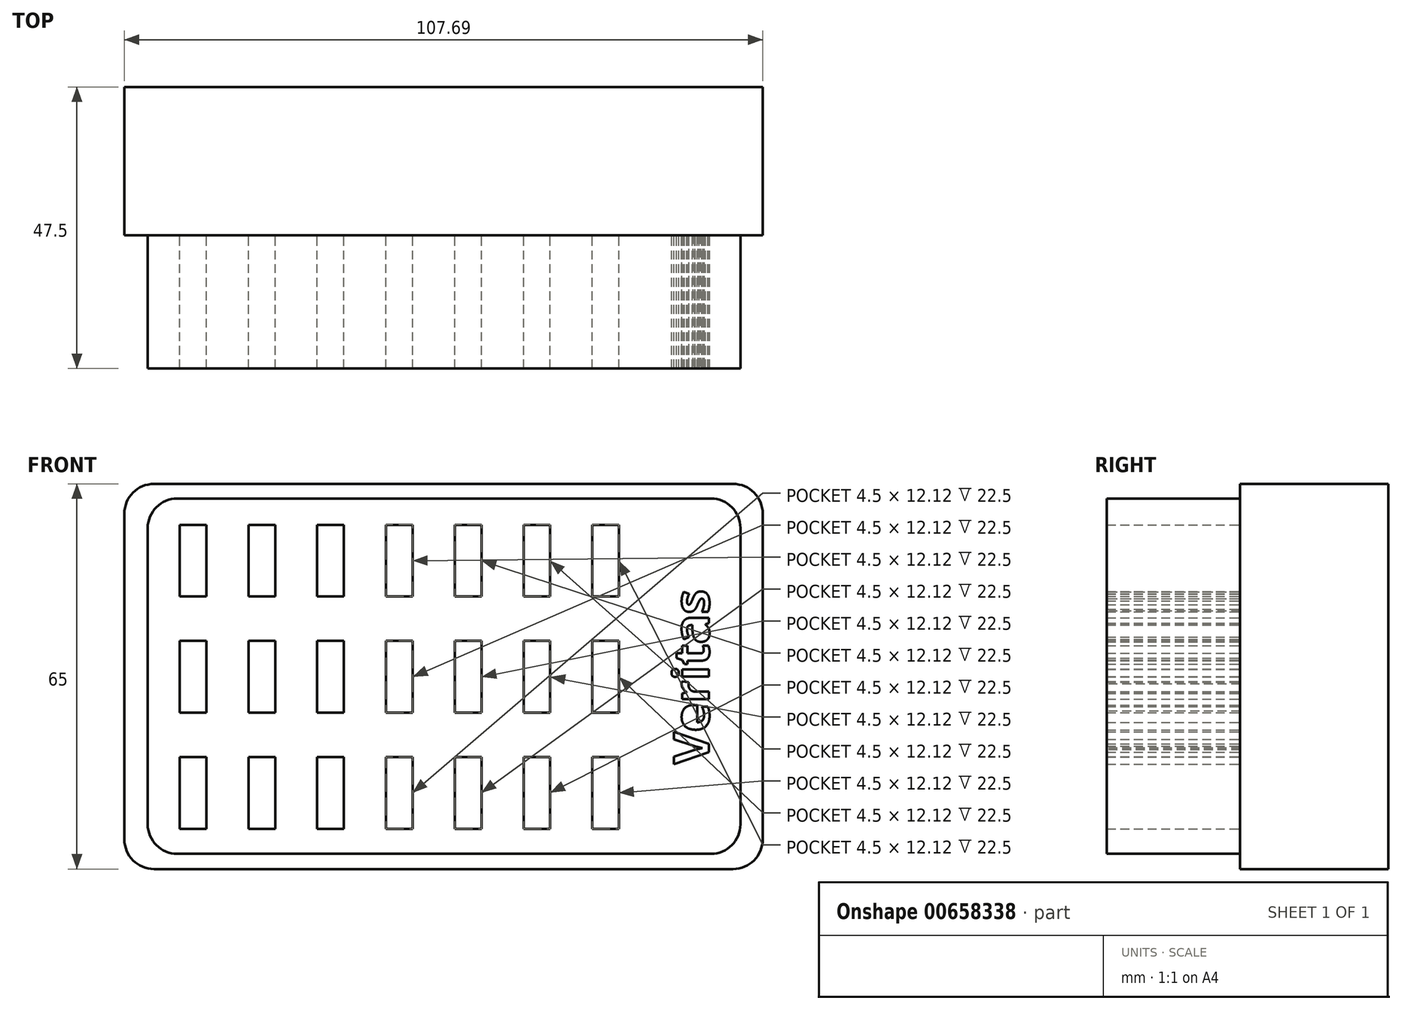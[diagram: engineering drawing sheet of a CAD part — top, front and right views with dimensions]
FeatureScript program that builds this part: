
annotation { "Feature Type Name" : "Feature", "Feature Type Description" : "" }
export const myFeature = defineFeature(function(context is Context, id is Id, definition is map)
    precondition{}
    {
        {
            var Q0;
            Q0=qCreatedBy(makeId("Front.planeOp"),FACE);
            var sketch = newSketch(context, id + "F0", { "sketchPlane" : qUnion([Q0])});
            skLineSegment(sketch, "E0.bottom", {"start": v(50, 30) * mm, "end": v(-50, 30) * mm});
            skLineSegment(sketch, "E0.top", {"start": v(50, -30) * mm, "end": v(-50, -30) * mm});
            skLineSegment(sketch, "E0.left", {"start": v(50, 30) * mm, "end": v(50, -30) * mm});
            skLineSegment(sketch, "E0.right", {"start": v(-50, 30) * mm, "end": v(-50, -30) * mm});
            skPoint(sketch, "E0.middle", {"position": v(0, 0) * mm});
            skLineSegment(sketch, "E1.bottom", {"start": v(-44.6, -13.64) * mm, "end": v(-40.1, -13.64) * mm});
            skLineSegment(sketch, "E1.top", {"start": v(-44.6, -25.76) * mm, "end": v(-40.1, -25.76) * mm});
            skLineSegment(sketch, "E1.left", {"start": v(-44.6, -13.64) * mm, "end": v(-44.6, -25.76) * mm});
            skLineSegment(sketch, "E1.right", {"start": v(-40.1, -13.64) * mm, "end": v(-40.1, -25.76) * mm});
            skLineSegment(sketch, "E2.0.1.0", {"start": v(-40.1, 5.96) * mm, "end": v(-40.1, -6.16) * mm});
            skLineSegment(sketch, "E2.0.1.1", {"start": v(-44.6, 5.96) * mm, "end": v(-44.6, -6.16) * mm});
            skLineSegment(sketch, "E2.0.1.2", {"start": v(-44.6, -6.16) * mm, "end": v(-40.1, -6.16) * mm});
            skLineSegment(sketch, "E2.0.1.3", {"start": v(-44.6, 5.96) * mm, "end": v(-40.1, 5.96) * mm});
            skLineSegment(sketch, "E2.0.2.0", {"start": v(-40.1, 25.56) * mm, "end": v(-40.1, 13.44) * mm});
            skLineSegment(sketch, "E2.0.2.1", {"start": v(-44.6, 25.56) * mm, "end": v(-44.6, 13.44) * mm});
            skLineSegment(sketch, "E2.0.2.2", {"start": v(-44.6, 13.44) * mm, "end": v(-40.1, 13.44) * mm});
            skLineSegment(sketch, "E2.0.2.3", {"start": v(-44.6, 25.56) * mm, "end": v(-40.1, 25.56) * mm});
            skLineSegment(sketch, "E2.1.0.0", {"start": v(-28.5, -13.64) * mm, "end": v(-28.5, -25.76) * mm});
            skLineSegment(sketch, "E2.1.0.1", {"start": v(-33, -13.64) * mm, "end": v(-33, -25.76) * mm});
            skLineSegment(sketch, "E2.1.0.2", {"start": v(-33, -25.76) * mm, "end": v(-28.5, -25.76) * mm});
            skLineSegment(sketch, "E2.1.0.3", {"start": v(-33, -13.64) * mm, "end": v(-28.5, -13.64) * mm});
            skLineSegment(sketch, "E2.1.1.0", {"start": v(-28.5, 5.96) * mm, "end": v(-28.5, -6.16) * mm});
            skLineSegment(sketch, "E2.1.1.1", {"start": v(-33, 5.96) * mm, "end": v(-33, -6.16) * mm});
            skLineSegment(sketch, "E2.1.1.2", {"start": v(-33, -6.16) * mm, "end": v(-28.5, -6.16) * mm});
            skLineSegment(sketch, "E2.1.1.3", {"start": v(-33, 5.96) * mm, "end": v(-28.5, 5.96) * mm});
            skLineSegment(sketch, "E2.1.2.0", {"start": v(-28.5, 25.56) * mm, "end": v(-28.5, 13.44) * mm});
            skLineSegment(sketch, "E2.1.2.1", {"start": v(-33, 25.56) * mm, "end": v(-33, 13.44) * mm});
            skLineSegment(sketch, "E2.1.2.2", {"start": v(-33, 13.44) * mm, "end": v(-28.5, 13.44) * mm});
            skLineSegment(sketch, "E2.1.2.3", {"start": v(-33, 25.56) * mm, "end": v(-28.5, 25.56) * mm});
            skLineSegment(sketch, "E2.2.0.0", {"start": v(-16.9, -13.64) * mm, "end": v(-16.9, -25.76) * mm});
            skLineSegment(sketch, "E2.2.0.1", {"start": v(-21.4, -13.64) * mm, "end": v(-21.4, -25.76) * mm});
            skLineSegment(sketch, "E2.2.0.2", {"start": v(-21.4, -25.76) * mm, "end": v(-16.9, -25.76) * mm});
            skLineSegment(sketch, "E2.2.0.3", {"start": v(-21.4, -13.64) * mm, "end": v(-16.9, -13.64) * mm});
            skLineSegment(sketch, "E2.2.1.0", {"start": v(-16.9, 5.96) * mm, "end": v(-16.9, -6.16) * mm});
            skLineSegment(sketch, "E2.2.1.1", {"start": v(-21.4, 5.96) * mm, "end": v(-21.4, -6.16) * mm});
            skLineSegment(sketch, "E2.2.1.2", {"start": v(-21.4, -6.16) * mm, "end": v(-16.9, -6.16) * mm});
            skLineSegment(sketch, "E2.2.1.3", {"start": v(-21.4, 5.96) * mm, "end": v(-16.9, 5.96) * mm});
            skLineSegment(sketch, "E2.2.2.0", {"start": v(-16.9, 25.56) * mm, "end": v(-16.9, 13.44) * mm});
            skLineSegment(sketch, "E2.2.2.1", {"start": v(-21.4, 25.56) * mm, "end": v(-21.4, 13.44) * mm});
            skLineSegment(sketch, "E2.2.2.2", {"start": v(-21.4, 13.44) * mm, "end": v(-16.9, 13.44) * mm});
            skLineSegment(sketch, "E2.2.2.3", {"start": v(-21.4, 25.56) * mm, "end": v(-16.9, 25.56) * mm});
            skLineSegment(sketch, "E2.3.0.0", {"start": v(-5.3, -13.64) * mm, "end": v(-5.3, -25.76) * mm});
            skLineSegment(sketch, "E2.3.0.1", {"start": v(-9.8, -13.64) * mm, "end": v(-9.8, -25.76) * mm});
            skLineSegment(sketch, "E2.3.0.2", {"start": v(-9.8, -25.76) * mm, "end": v(-5.3, -25.76) * mm});
            skLineSegment(sketch, "E2.3.0.3", {"start": v(-9.8, -13.64) * mm, "end": v(-5.3, -13.64) * mm});
            skLineSegment(sketch, "E2.3.1.0", {"start": v(-5.3, 5.96) * mm, "end": v(-5.3, -6.16) * mm});
            skLineSegment(sketch, "E2.3.1.1", {"start": v(-9.8, 5.96) * mm, "end": v(-9.8, -6.16) * mm});
            skLineSegment(sketch, "E2.3.1.2", {"start": v(-9.8, -6.16) * mm, "end": v(-5.3, -6.16) * mm});
            skLineSegment(sketch, "E2.3.1.3", {"start": v(-9.8, 5.96) * mm, "end": v(-5.3, 5.96) * mm});
            skLineSegment(sketch, "E2.3.2.0", {"start": v(-5.3, 25.56) * mm, "end": v(-5.3, 13.44) * mm});
            skLineSegment(sketch, "E2.3.2.1", {"start": v(-9.8, 25.56) * mm, "end": v(-9.8, 13.44) * mm});
            skLineSegment(sketch, "E2.3.2.2", {"start": v(-9.8, 13.44) * mm, "end": v(-5.3, 13.44) * mm});
            skLineSegment(sketch, "E2.3.2.3", {"start": v(-9.8, 25.56) * mm, "end": v(-5.3, 25.56) * mm});
            skLineSegment(sketch, "E2.4.0.0", {"start": v(6.3, -13.64) * mm, "end": v(6.3, -25.76) * mm});
            skLineSegment(sketch, "E2.4.0.1", {"start": v(1.8, -13.64) * mm, "end": v(1.8, -25.76) * mm});
            skLineSegment(sketch, "E2.4.0.2", {"start": v(1.8, -25.76) * mm, "end": v(6.3, -25.76) * mm});
            skLineSegment(sketch, "E2.4.0.3", {"start": v(1.8, -13.64) * mm, "end": v(6.3, -13.64) * mm});
            skLineSegment(sketch, "E2.4.1.0", {"start": v(6.3, 5.96) * mm, "end": v(6.3, -6.16) * mm});
            skLineSegment(sketch, "E2.4.1.1", {"start": v(1.8, 5.96) * mm, "end": v(1.8, -6.16) * mm});
            skLineSegment(sketch, "E2.4.1.2", {"start": v(1.8, -6.16) * mm, "end": v(6.3, -6.16) * mm});
            skLineSegment(sketch, "E2.4.1.3", {"start": v(1.8, 5.96) * mm, "end": v(6.3, 5.96) * mm});
            skLineSegment(sketch, "E2.4.2.0", {"start": v(6.3, 25.56) * mm, "end": v(6.3, 13.44) * mm});
            skLineSegment(sketch, "E2.4.2.1", {"start": v(1.8, 25.56) * mm, "end": v(1.8, 13.44) * mm});
            skLineSegment(sketch, "E2.4.2.2", {"start": v(1.8, 13.44) * mm, "end": v(6.3, 13.44) * mm});
            skLineSegment(sketch, "E2.4.2.3", {"start": v(1.8, 25.56) * mm, "end": v(6.3, 25.56) * mm});
            skLineSegment(sketch, "E2.5.0.0", {"start": v(17.9, -13.64) * mm, "end": v(17.9, -25.76) * mm});
            skLineSegment(sketch, "E2.5.0.1", {"start": v(13.4, -13.64) * mm, "end": v(13.4, -25.76) * mm});
            skLineSegment(sketch, "E2.5.0.2", {"start": v(13.4, -25.76) * mm, "end": v(17.9, -25.76) * mm});
            skLineSegment(sketch, "E2.5.0.3", {"start": v(13.4, -13.64) * mm, "end": v(17.9, -13.64) * mm});
            skLineSegment(sketch, "E2.5.1.0", {"start": v(17.9, 5.96) * mm, "end": v(17.9, -6.16) * mm});
            skLineSegment(sketch, "E2.5.1.1", {"start": v(13.4, 5.96) * mm, "end": v(13.4, -6.16) * mm});
            skLineSegment(sketch, "E2.5.1.2", {"start": v(13.4, -6.16) * mm, "end": v(17.9, -6.16) * mm});
            skLineSegment(sketch, "E2.5.1.3", {"start": v(13.4, 5.96) * mm, "end": v(17.9, 5.96) * mm});
            skLineSegment(sketch, "E2.5.2.0", {"start": v(17.9, 25.56) * mm, "end": v(17.9, 13.44) * mm});
            skLineSegment(sketch, "E2.5.2.1", {"start": v(13.4, 25.56) * mm, "end": v(13.4, 13.44) * mm});
            skLineSegment(sketch, "E2.5.2.2", {"start": v(13.4, 13.44) * mm, "end": v(17.9, 13.44) * mm});
            skLineSegment(sketch, "E2.5.2.3", {"start": v(13.4, 25.56) * mm, "end": v(17.9, 25.56) * mm});
            skLineSegment(sketch, "E2.6.0.0", {"start": v(29.5, -13.64) * mm, "end": v(29.5, -25.76) * mm});
            skLineSegment(sketch, "E2.6.0.1", {"start": v(25, -13.64) * mm, "end": v(25, -25.76) * mm});
            skLineSegment(sketch, "E2.6.0.2", {"start": v(25, -25.76) * mm, "end": v(29.5, -25.76) * mm});
            skLineSegment(sketch, "E2.6.0.3", {"start": v(25, -13.64) * mm, "end": v(29.5, -13.64) * mm});
            skLineSegment(sketch, "E2.6.1.0", {"start": v(29.5, 5.96) * mm, "end": v(29.5, -6.16) * mm});
            skLineSegment(sketch, "E2.6.1.1", {"start": v(25, 5.96) * mm, "end": v(25, -6.16) * mm});
            skLineSegment(sketch, "E2.6.1.2", {"start": v(25, -6.16) * mm, "end": v(29.5, -6.16) * mm});
            skLineSegment(sketch, "E2.6.1.3", {"start": v(25, 5.96) * mm, "end": v(29.5, 5.96) * mm});
            skLineSegment(sketch, "E2.6.2.0", {"start": v(29.5, 25.56) * mm, "end": v(29.5, 13.44) * mm});
            skLineSegment(sketch, "E2.6.2.1", {"start": v(25, 25.56) * mm, "end": v(25, 13.44) * mm});
            skLineSegment(sketch, "E2.6.2.2", {"start": v(25, 13.44) * mm, "end": v(29.5, 13.44) * mm});
            skLineSegment(sketch, "E2.6.2.3", {"start": v(25, 25.56) * mm, "end": v(29.5, 25.56) * mm});
            skLineSegment(sketch, "E2.direction1", {"start": v(-44.6, -25.76) * mm, "end": v(-33, -25.76) * mm, "construction": true});
            skLineSegment(sketch, "E2.direction2", {"start": v(-44.6, -25.76) * mm, "end": v(-44.6, -6.16) * mm, "construction": true});
            skText(sketch, "E3", { "text": "Veritas\n", "fontName": "OpenSans-Bold.ttf"});
            const initialGuessF0  = {"E3": [0.0447, -0.01484, 0, 1, 0.006]};
            skSetInitialGuess(sketch, initialGuessF0);
            skSolve(sketch);
        }
        {
            var Q0;
            Q0=makeQuery(id+"F0.imprint","IMPRINT",FACE,{"disambiguationData":[TD([[makeQuery(id+"F0.imprint","IMPRINT",EDGE,{"derivedFrom":sQuery(id+"F0.wireOp",EDGE,"E0.bottom")}),1.0]])]});
            extrude(context, id + "F1", {"entities" : qUnion([Q0]), "depth" : 35 * mm, "offsetDistance" : 25 * mm});
        }
        {
            var Q0;
            Q0=qCreatedBy(makeId("Front.planeOp"),FACE);
            var sketch = newSketch(context, id + "F2", { "sketchPlane" : qUnion([Q0])});
            skLineSegment(sketch, "E4.bottom", {"start": v(53.75, 32.45) * mm, "end": v(-53.94, 32.45) * mm});
            skLineSegment(sketch, "E4.top", {"start": v(53.75, -32.55) * mm, "end": v(-53.94, -32.55) * mm});
            skLineSegment(sketch, "E4.left", {"start": v(53.75, 32.45) * mm, "end": v(53.75, -32.55) * mm});
            skLineSegment(sketch, "E4.right", {"start": v(-53.94, 32.45) * mm, "end": v(-53.94, -32.55) * mm});
            skSolve(sketch);
        }
        {
            var Q0;
            Q0=qSketchRegion(id+"F2",true);
            extrude(context, id + "F3", {"entities" : qUnion([Q0]), "operationType" : NewBodyOperationType.ADD, "endBound" : BoundingType.SYMMETRIC, "depth" : 25 * mm, "offsetDistance" : 25 * mm});
        }
        {
            var Q0;
            Q0=makeQuery(id+"F1.opExtrude","SWEPT_EDGE",EDGE,{"disambiguationData":[OSD([sQuery(id+"F0.wireOp",EDGE,"E0.top"),sQuery(id+"F0.wireOp",EDGE,"E0.right")])]});
            var Q1;
            Q1=makeQuery(id+"F1.opExtrude","SWEPT_EDGE",EDGE,{"disambiguationData":[OSD([sQuery(id+"F0.wireOp",EDGE,"E0.top"),sQuery(id+"F0.wireOp",EDGE,"E0.left")])]});
            var Q2;
            Q2=makeQuery(id+"F1.opExtrude","SWEPT_EDGE",EDGE,{"disambiguationData":[OSD([sQuery(id+"F0.wireOp",EDGE,"E0.bottom"),sQuery(id+"F0.wireOp",EDGE,"E0.left")])]});
            var Q3;
            Q3=makeQuery(id+"F1.opExtrude","SWEPT_EDGE",EDGE,{"disambiguationData":[OSD([sQuery(id+"F0.wireOp",EDGE,"E0.bottom"),sQuery(id+"F0.wireOp",EDGE,"E0.right")])]});
            var Q4;
            Q4=makeQuery(id+"F3.opExtrude","SWEPT_EDGE",EDGE,{"disambiguationData":[OSD([sQuery(id+"F2.wireOp",EDGE,"E4.top"),sQuery(id+"F2.wireOp",EDGE,"E4.right")])]});
            var Q5;
            Q5=makeQuery(id+"F3.opExtrude","SWEPT_EDGE",EDGE,{"disambiguationData":[OSD([sQuery(id+"F2.wireOp",EDGE,"E4.top"),sQuery(id+"F2.wireOp",EDGE,"E4.left")])]});
            var Q6;
            Q6=makeQuery(id+"F3.opExtrude","SWEPT_EDGE",EDGE,{"disambiguationData":[OSD([sQuery(id+"F2.wireOp",EDGE,"E4.bottom"),sQuery(id+"F2.wireOp",EDGE,"E4.left")])]});
            var Q7;
            Q7=makeQuery(id+"F3.opExtrude","SWEPT_EDGE",EDGE,{"disambiguationData":[OSD([sQuery(id+"F2.wireOp",EDGE,"E4.bottom"),sQuery(id+"F2.wireOp",EDGE,"E4.right")])]});
            fillet(context, id + "F4", {"entities" : qUnion([Q0, Q1, Q2, Q3, Q4, Q5, Q6, Q7]), "radius" : 5 * mm, "tangentPropagation" : true, "allowEdgeOverflow" : false});
        }
    });
